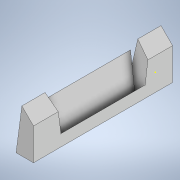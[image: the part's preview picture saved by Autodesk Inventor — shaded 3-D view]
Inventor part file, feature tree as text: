
AUTODESK INVENTOR PART (.ipt)
format: ipt  version: 2021 (Build 250183000, 183)  size: 170,496 bytes
history: native  units: in
note: dims shown in document units (in); Inventor stores cm internally (conversion verified against a paired STEP export)
features: sketch x8, extrude x7, projected_geometry x7
ambient origin geometry x8: Origin, YZ Plane, XZ Plane, XY Plane, X Axis, Y Axis, Z Axis, Center Point
bodies: Solid1 (feature_tree)
feature tree (22):
  extrude  "Extrusion1"  Depth=0.2362in
  extrude  "Extrusion2"  Depth=0.1181in
  extrude  "Extrusion3"  Depth=0.1181in
  extrude  "Extrusion4"  Depth=0.3937in TaperAngle=0.0deg
  extrude  "Extrusion5"  Depth=0.9188in TaperAngle=0.0deg
  extrude  "Extrusion6"  Depth=0.0787in
  extrude  "Extrusion7"  Depth=0.8312in TaperAngle=0.0deg
  sketch  "Sketch9"  dims[d27=0.1575in d28=0.0394in]
  sketch  "Sketch1"  dims[d0=0.2362in d3=0.4331in]
  sketch  "Sketch2"  dims[d4=0.3937in d5=0.0in d6=0.1181in]
  sketch  "Sketch3"  dims[d7=0.4331in d8=0.1181in]
  projected_geometry  "Projected Loop1"
  sketch  "Sketch4"  dims[d9=1.1024in d10=0.0in d11=0.3937in d12=0.0in]
  sketch  "Sketch5"  dims[d14=0.0787in d16=0.9188in d17=0.0in]
  projected_geometry  "Projected Loop2"
  sketch  "Sketch6"  dims[d18=0.9188in d19=0.0in d20=0.0787in]
  projected_geometry  "Projected Loop3"
  projected_geometry  "Projected Loop4"
  sketch  "Sketch7"  dims[d21=0.8312in d22=0.0in d23=0.8312in d24=0.0in]
  projected_geometry  "Projected Loop5"
  projected_geometry  "Projected Loop7"
  projected_geometry  "Projected Loop8"
